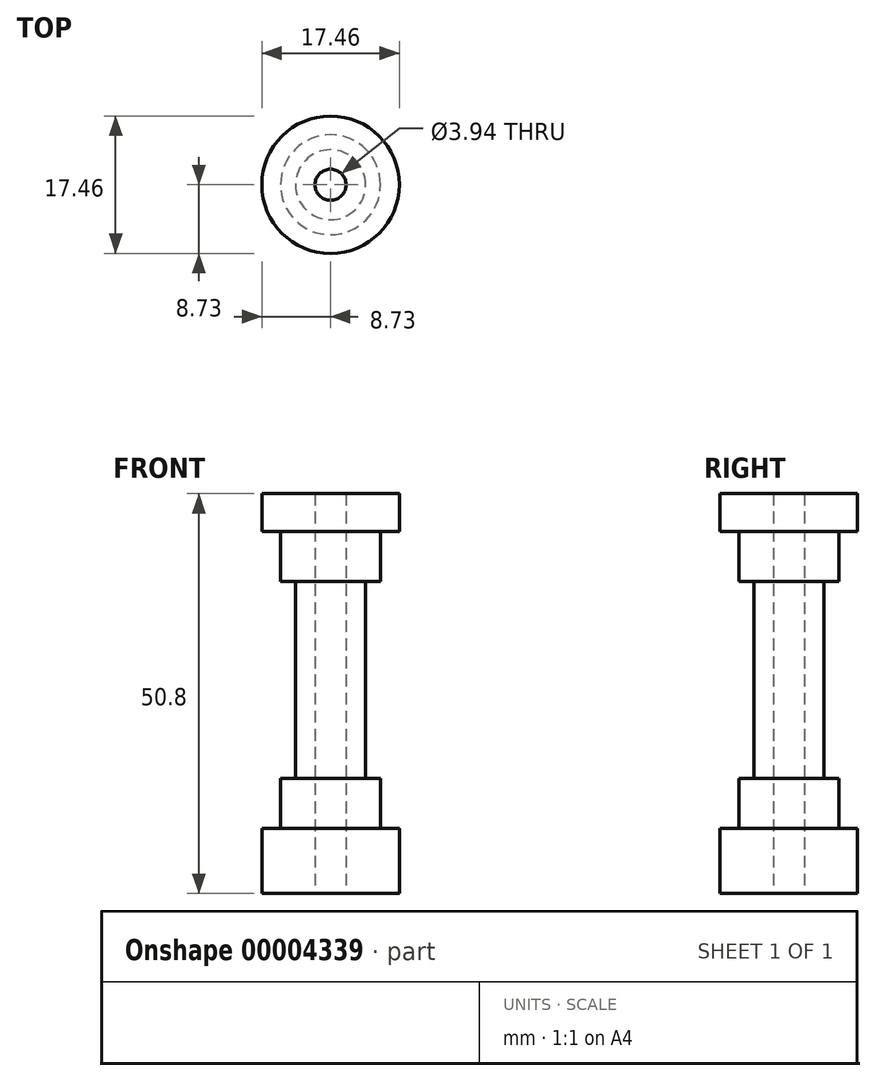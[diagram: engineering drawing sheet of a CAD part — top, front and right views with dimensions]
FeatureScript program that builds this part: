
annotation { "Feature Type Name" : "Feature", "Feature Type Description" : "" }
export const myFeature = defineFeature(function(context is Context, id is Id, definition is map)
    precondition{}
    {
        {
            var Q0;
            Q0=qCreatedBy(makeId("Top.planeOp"),FACE);
            var sketch = newSketch(context, id + "F0", { "sketchPlane" : qUnion([Q0])});
            skCircle(sketch, "E0", {"center": v(0, 0) * mm, "radius": 8.73 * mm});
            skCircle(sketch, "E1", {"center": v(0, 0) * mm, "radius": 6.35 * mm});
            skCircle(sketch, "E2", {"center": v(0, 0) * mm, "radius": 1.97 * mm});
            skCircle(sketch, "E3", {"center": v(0, 0) * mm, "radius": 4.45 * mm});
            skSolve(sketch);
        }
        {
            var Q0;
            Q0=makeQuery(id+"F0.imprint","IMPRINT",FACE,{"disambiguationData":[TD([[makeQuery(id+"F0.imprint","IMPRINT",EDGE,{"derivedFrom":sQuery(id+"F0.wireOp",EDGE,"E2")}),-1.0]])]});
            extrude(context, id + "F1", {"entities" : qUnion([Q0]), "depth" : 50.8 * mm});
        }
        {
            var Q0;
            Q0=makeQuery(id+"F0.imprint","IMPRINT",FACE,{"disambiguationData":[TD([[makeQuery(id+"F0.imprint","IMPRINT",EDGE,{"derivedFrom":sQuery(id+"F0.wireOp",EDGE,"E1")}),1.0]])]});
            extrude(context, id + "F2", {"entities" : qUnion([Q0]), "operationType" : NewBodyOperationType.ADD, "depth" : 14.6 * mm});
        }
        {
            var Q0;
            Q0=makeQuery(id+"F0.imprint","IMPRINT",FACE,{"disambiguationData":[TD([[makeQuery(id+"F0.imprint","IMPRINT",EDGE,{"derivedFrom":sQuery(id+"F0.wireOp",EDGE,"E1")}),1.0]])]});
            var Q1;
            Q1=makeQuery(id+"F0.imprint","IMPRINT",FACE,{"disambiguationData":[TD([[makeQuery(id+"F0.imprint","IMPRINT",EDGE,{"derivedFrom":sQuery(id+"F0.wireOp",EDGE,"E0")}),1.0]])]});
            extrude(context, id + "F3", {"entities" : qUnion([Q0, Q1]), "operationType" : NewBodyOperationType.ADD, "depth" : 8.25 * mm});
        }
        {
            var Q0;
            Q0=makeQuery(id+"F1.opExtrude","CAP_FACE",FACE,{"disambiguationData":[OSD([sQuery(id+"F0.wireOp",EDGE,"E2"),sQuery(id+"F0.wireOp",EDGE,"E3")])],"isStart":false});
            var sketch = newSketch(context, id + "F4", { "sketchPlane" : qUnion([Q0])});
            skCircle(sketch, "E4", {"center": v(0, 0) * mm, "radius": 8.73 * mm});
            skCircle(sketch, "E5", {"center": v(0, 0) * mm, "radius": 6.35 * mm});
            skCircle(sketch, "E6", {"center": v(0, 0) * mm, "radius": 1.97 * mm});
            skCircle(sketch, "E7", {"center": v(0, 0) * mm, "radius": 4.45 * mm});
            skSolve(sketch);
        }
        {
            var Q0;
            Q0=makeQuery(id+"F4.imprint","IMPRINT",FACE,{"disambiguationData":[TD([[makeQuery(id+"F4.imprint","IMPRINT",EDGE,{"derivedFrom":sQuery(id+"F4.wireOp",EDGE,"E5")}),1.0]])]});
            var Q1;
            Q1=sQuery(id+"F4.wireOp",EDGE,"E4");
            var Q2;
            Q2=sQuery(id+"F4.wireOp",EDGE,"E5");
            var Q3;
            Q3=sQuery(id+"F4.wireOp",EDGE,"E6");
            var Q4;
            Q4=sQuery(id+"F4.wireOp",EDGE,"E7");
            extrude(context, id + "F5", {"entities" : qUnion([Q0]), "operationType" : NewBodyOperationType.ADD, "surfaceEntities" : qUnion([Q1, Q2, Q3, Q4]), "oppositeDirection" : true, "depth" : 11.18 * mm});
        }
        {
            var Q0;
            Q0=makeQuery(id+"F4.imprint","IMPRINT",FACE,{"disambiguationData":[TD([[makeQuery(id+"F4.imprint","IMPRINT",EDGE,{"derivedFrom":sQuery(id+"F4.wireOp",EDGE,"E4")}),1.0]])]});
            extrude(context, id + "F6", {"entities" : qUnion([Q0]), "operationType" : NewBodyOperationType.ADD, "oppositeDirection" : true, "depth" : 4.83 * mm});
        }
    });
